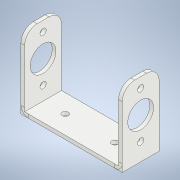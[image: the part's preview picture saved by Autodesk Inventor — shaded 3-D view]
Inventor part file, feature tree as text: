
AUTODESK INVENTOR PART (.ipt)
format: ipt  version: 2022 (Build 260153000, 153)  size: 220,672 bytes
history: native  units: in
note: dims shown in document units (in); Inventor stores cm internally (conversion verified against a paired STEP export)
features: sketch x5, sheet_metal_op x4, projected_geometry x4, hole x3, extrude x2, other x2, fillet x1
ambient origin geometry x8: Origin, YZ Plane, XZ Plane, XY Plane, X Axis, Y Axis, Z Axis, Center Point
bodies: Body1 (feature_tree)
feature tree (21):
  sheet_metal_op  "Face1"
  sheet_metal_op  "Flange1"
  sketch  "Sketch5"  dims[d14=0.16in d15=0.08in]
  hole  "Hole1"  [1 undecoded]
  hole  "Hole2"  [1 undecoded]
  fillet  "Fillet1"  Radius=0.04in
  hole  "Hole3"  [1 undecoded]
  sketch  "Sketch7"  dims[d20=0.08in d21=0.08in d22=0.4921in d23=0.4921in d24=0.1339in d25=0.2362in d26=0.2559in d27=0.1181in d28=0.6181in d29=0.08in d30=0.8108in d31=0.5512in d32=0.2362in d33=0.1575in d34=0.0787in d35=90.0deg d36=0.315in d37=0.8108in d38=0.2662in d39=0.3937in d40=0.1339in d41=0.2362in d42=0.2559in d43=0.1181in d44=90.0deg d45=0.315in d46=0.8108in d47=0.0in d48=0.0in d49=0.3937in d50=0.0in d7=0.0197in d8=1.9685in]
  extrude  "Extrusion3"  Depth=0.08in
  extrude  "Extrusion4"  Depth=0.08in
  sketch  "Sketch3"  dims[d9=2.1654in d10=0.7874in]
  other  "Plate1"
  sketch  "Sketch4"  dims[d11=0.08in d12=0.08in d13=0.04in]
  other  "Plate2"
  sheet_metal_op  "Bend1"
  sheet_metal_op  "Corner1"
  projected_geometry  "Projected Loop3"
  sketch  "Sketch6"  dims[d16=1.5748in d17=90.0deg d18=0.08in d19=0.32in]
  projected_geometry  "Projected Loop4"
  projected_geometry  "Projected Loop5"
  projected_geometry  "Projected Loop6"
note: 3 required parameter values undecoded (feature->parameter linkage not recoverable at this tier; creation-order binding heuristic only, values carry confidence <= 0.55)
